# Revit family: BOS-Leibungszarge-Planar-QTUsd-MW_Familie
name_source: partatom
category: Türen
revit_build: Autodesk Revit 2017 (Build: 20160225_1515(x64)
units: mm (PartAtom-declared; Revit-internal decimal feet)

## family parameters
Basisbauteil = Wand
Beim Laden mit Abzugskörper schneiden = Nein
Gemeinsam genutzt = Nein
Immer vertikal = Ja
Raumberechnungspunkt = Ja

## types (2) — shared parameters
BBL1 Bandbezugslinie   Hinge Position 1 = 241 mm  [stored 0.790682 ft]
BE max. = 100 mm  [stored 0.328084 ft]
Bauelement = BOS Stahlzarge
Dichtung 1 = Ja
Doppelfalz = Nein
Drehpunkt Warnung sichtbar = Ja
Drehpunktabstand (FM) horizontal = 2.5 mm  [stored 0.0082021 ft]
Drehpunktabstand (SP) vertikal = 13.5 mm  [stored 0.0442913 ft]
Drehpunktreferenz horizontal = 500 mm  [stored 1.64042 ft]
Einfachfalz = Ja
FMB max. = 1341 mm  [stored 4.39961 ft]
FMB min. = 591 mm  [stored 1.93898 ft]
FMH max. = 2858 mm  [stored 9.37664 ft]
FMH min. = 1608 mm  [stored 5.27559 ft]
Falzaufschlag = 15 mm  [stored 0.0492126 ft]
Falzaufschlag gesamt = 15 mm  [stored 0.0492126 ft]
Falztiefe = 46.5 mm  [stored 0.152559 ft]
Falztiefe 2 = 23 mm  [stored 0.0754593 ft]
Falztiefe gesamt = 46.5 mm  [stored 0.152559 ft]
Funktion = Innen
GT max. = 650 mm  [stored 2.13255 ft]
Gefälzt = Nein
Hersteller = BOS GmbH Best Of Steel, Lütkenfelde 4, D-48282 Emsdetten
Info-Texte sichtbar = Ja
Information in English = Nein
Material = grundiert, feuerverzinktes Feinblech nach DIN EN 10143
Material - Bänder = <Nach Kategorie>
Material - Dichtung = <Nach Kategorie>
Material - Drückergarnitur = <Nach Kategorie>
Material - Türblatt = <Nach Kategorie>
Material - Zarge = <Nach Kategorie>
Modell = QTUsd
Profilverschiebung = 15 mm  [stored 0.0492126 ft]
Putzwinkel max. = 28 mm  [stored 0.0918635 ft]
Putzwinkel min. = 10 mm  [stored 0.0328084 ft]
Sickentiefe = 10 mm  [stored 0.0328084 ft]
Spiegel hinten max. = 80 mm  [stored 0.262467 ft]
Spiegel hinten min. = 30 mm  [stored 0.0984252 ft]
Spiegel innen max. = 75 mm  [stored 0.246063 ft]
Spiegel vorne max. = 60 mm  [stored 0.19685 ft]
Stumpf = Ja
Technische Infos rund um die Stahlzarge = www.BestOfSteel.de/tools-downloads/technische-infos-rund-um-die-stahlzarge/
Türblattabstand 1 = -2 mm  [stored -0.00656168 ft]
Türblattabstand 2 = 4.5 mm  [stored 0.0147638 ft]
Türblattabstand 3 = 4.5 mm  [stored 0.0147638 ft]
Türblattabstand links-rechts = 3.5 mm  [stored 0.0114829 ft]
Türblattabstand oben = 4 mm  [stored 0.0131234 ft]
Türblattabstand unten = 7 mm  [stored 0.0229659 ft]
Türblattaufschlag = 13 mm
Türblattstärke = 65 mm  [stored 0.213255 ft]
Türblattstärke 2 = 40 mm  [stored 0.131234 ft]
Türblattstärke 3 = 25 mm  [stored 0.082021 ft]
Türblattversatz  horizontal = 6 mm  [stored 0.019685 ft]
Türblattversatz vertikal = 15.5 mm  [stored 0.050853 ft]
URL = www.BestOfSteel.de/stahlzargen/sonderzargen-fuer-drehfluegeltueren/leibungszargen-planar/
Öffnungswinkel max. = 180.00°
Öffnungswinkel min. = 0.00°
zero-valued in all types: Breite, Dicke, Rohbaubreite, Rohbauhöhe, Türblattstärke 1

## per-type parameters (varying)
| type | Beschreibung | QTUsd (Bandrolle sichtbar) | QTUsd (versteckt liegendes Band) |
| QTUsd (Bandrolle sichtbar) | Leibungszarge Planar für Mauerwerk Variante 2, stumpf (Bandrolle sichtbar) | Ja | Nein |
| QTUsd (verdeckt liegendes Band) | Leibungszarge Planar für Mauerwerk Variante 2, stumpf (verdeckt liegendes Band) | Nein | Ja |

note: [stored X ft] marks values corroborated as IEEE doubles in the binary element streams (Revit-internal decimal feet)
